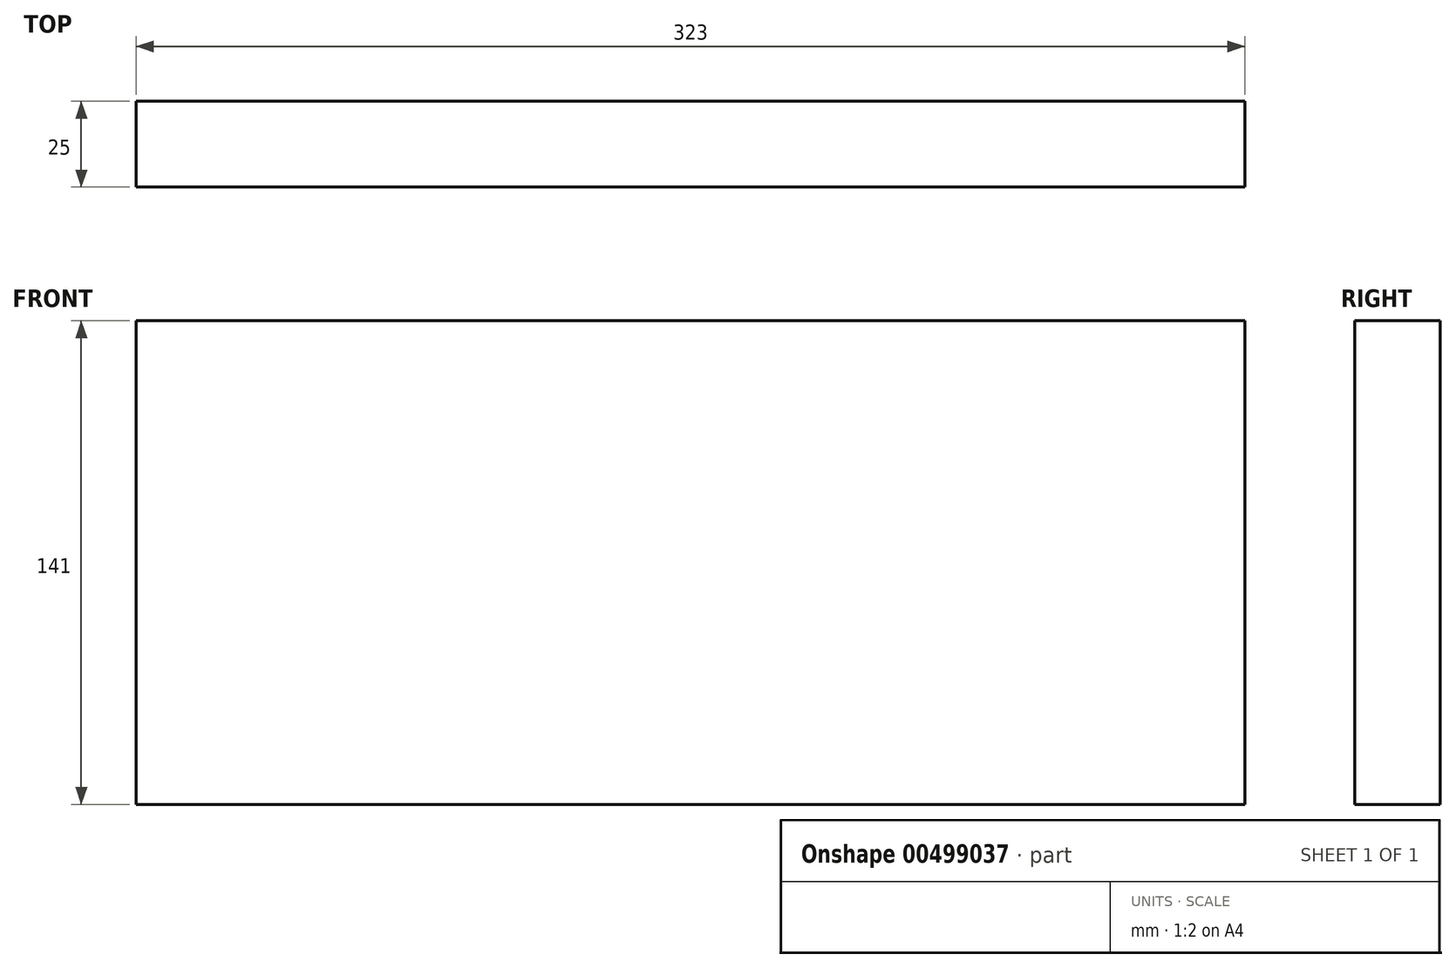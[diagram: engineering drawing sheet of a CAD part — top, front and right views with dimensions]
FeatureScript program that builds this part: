
annotation { "Feature Type Name" : "Feature", "Feature Type Description" : "" }
export const myFeature = defineFeature(function(context is Context, id is Id, definition is map)
    precondition{}
    {
        {
            var Q0;
            Q0=qCreatedBy(makeId("Front.planeOp"),FACE);
            var sketch = newSketch(context, id + "F0", { "sketchPlane" : qUnion([Q0])});
            skLineSegment(sketch, "E0.bottom", {"start": v(-133.87, 55.01) * mm, "end": v(189.13, 55.01) * mm});
            skLineSegment(sketch, "E0.top", {"start": v(-133.87, -85.99) * mm, "end": v(189.13, -85.99) * mm});
            skLineSegment(sketch, "E0.left", {"start": v(-133.87, 55.01) * mm, "end": v(-133.87, -85.99) * mm});
            skLineSegment(sketch, "E0.right", {"start": v(189.13, 55.01) * mm, "end": v(189.13, -85.99) * mm});
            skSolve(sketch);
        }
        {
            var Q0;
            Q0 = qSketchRegion(id + "F0", true);
            extrude(context, id + "F1", {"entities" : qUnion([Q0]), "depth" : 25 * mm, "offsetDistance" : 25 * mm});
        }
    });
